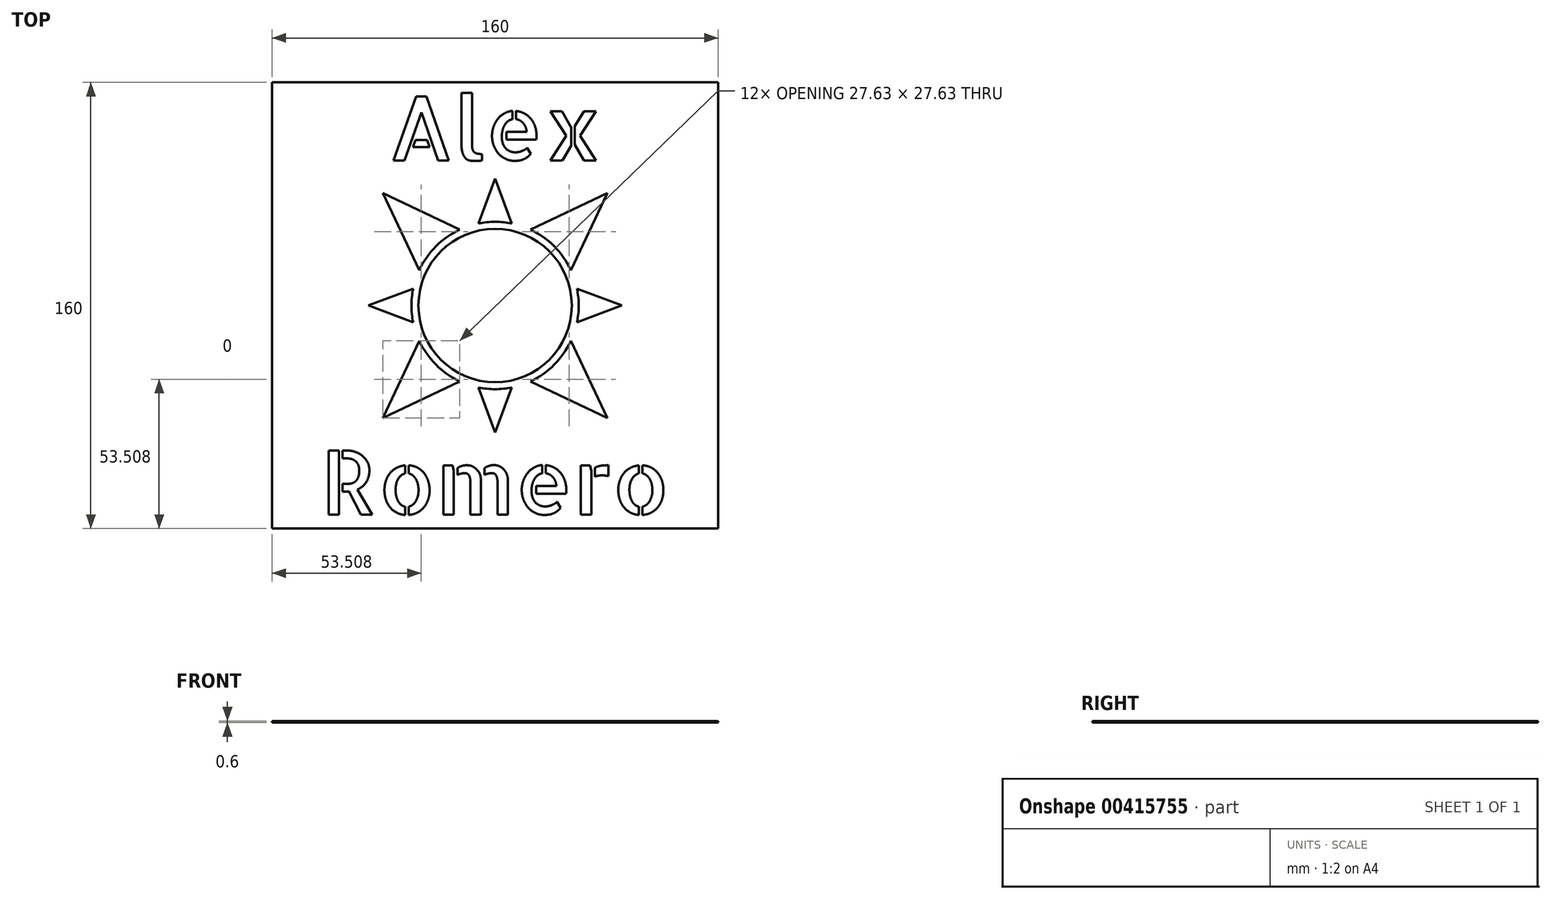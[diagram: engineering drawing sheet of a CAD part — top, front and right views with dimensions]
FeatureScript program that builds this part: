
annotation { "Feature Type Name" : "Feature", "Feature Type Description" : "" }
export const myFeature = defineFeature(function(context is Context, id is Id, definition is map)
    precondition{}
    {
        {
            var Q0;
            Q0=qCreatedBy(makeId("Top.planeOp"),FACE);
            var sketch = newSketch(context, id + "F0", { "sketchPlane" : qUnion([Q0])});
            skLineSegment(sketch, "E0.bottom", {"start": v(0, 0) * mm, "end": v(160, 0) * mm});
            skLineSegment(sketch, "E0.top", {"start": v(0, 160) * mm, "end": v(160, 160) * mm});
            skLineSegment(sketch, "E0.left", {"start": v(0, 0) * mm, "end": v(0, 160) * mm});
            skLineSegment(sketch, "E0.right", {"start": v(160, 0) * mm, "end": v(160, 160) * mm});
            skCircle(sketch, "E1", {"center": v(80, 80) * mm, "radius": 27.5 * mm});
            skLineSegment(sketch, "E2", {"start": v(0, 80) * mm, "end": v(160, 80) * mm, "construction": true});
            skLineSegment(sketch, "E3", {"start": v(80, 0) * mm, "end": v(80, 160) * mm, "construction": true});
            skText(sketch, "E4", { "text": "Alex", "fontName": "AllertaStencil-Regular.ttf"});
            skText(sketch, "E5", { "text": "Romero", "fontName": "AllertaStencil-Regular.ttf"});
            skArc(sketch, "E6", {"start": v(74, 109.4) * mm, "mid": v(80, 110) * mm, "end": v(86, 109.4) * mm});
            skLineSegment(sketch, "E7", {"start": v(74, 109.4) * mm, "end": v(80, 125.5) * mm});
            skLineSegment(sketch, "E8", {"start": v(80, 125.5) * mm, "end": v(86, 109.4) * mm});
            skLineSegment(sketch, "E9.1.0", {"start": v(109.4, 86) * mm, "end": v(125.5, 80) * mm});
            skLineSegment(sketch, "E9.1.1", {"start": v(125.5, 80) * mm, "end": v(109.4, 74) * mm});
            skArc(sketch, "E9.1.2", {"start": v(109.4, 86) * mm, "mid": v(110, 80) * mm, "end": v(109.4, 74) * mm});
            skLineSegment(sketch, "E9.2.0", {"start": v(86, 50.6) * mm, "end": v(80, 34.5) * mm});
            skLineSegment(sketch, "E9.2.1", {"start": v(80, 34.5) * mm, "end": v(74, 50.6) * mm});
            skArc(sketch, "E9.2.2", {"start": v(86, 50.6) * mm, "mid": v(80, 50) * mm, "end": v(74, 50.6) * mm});
            skLineSegment(sketch, "E9.3.0", {"start": v(50.6, 74) * mm, "end": v(34.5, 80) * mm});
            skLineSegment(sketch, "E9.3.1", {"start": v(34.5, 80) * mm, "end": v(50.6, 86) * mm});
            skArc(sketch, "E9.3.2", {"start": v(50.6, 74) * mm, "mid": v(50, 80) * mm, "end": v(50.6, 86) * mm});
            skLineSegment(sketch, "E9.anchor1", {"start": v(80, 80) * mm, "end": v(74, 109.4) * mm, "construction": true});
            skLineSegment(sketch, "E9.anchor2", {"start": v(80, 80) * mm, "end": v(50.6, 74) * mm, "construction": true});
            skLineSegment(sketch, "E10", {"start": v(80, 80) * mm, "end": v(33.62, 126.38) * mm, "construction": true});
            skLineSegment(sketch, "E11", {"start": v(80, 80) * mm, "end": v(42.08, 97.68) * mm, "construction": true});
            skLineSegment(sketch, "E12", {"start": v(80, 80) * mm, "end": v(62.27, 118.03) * mm, "construction": true});
            skArc(sketch, "E13", {"start": v(52.81, 92.68) * mm, "mid": v(58.79, 101.21) * mm, "end": v(67.32, 107.19) * mm});
            skLineSegment(sketch, "E14", {"start": v(52.81, 92.68) * mm, "end": v(39.7, 120.3) * mm});
            skLineSegment(sketch, "E15", {"start": v(39.7, 120.3) * mm, "end": v(67.32, 107.19) * mm});
            skLineSegment(sketch, "E16.1.0", {"start": v(67.32, 52.81) * mm, "end": v(39.7, 39.7) * mm});
            skLineSegment(sketch, "E16.1.1", {"start": v(39.7, 39.7) * mm, "end": v(52.81, 67.32) * mm});
            skArc(sketch, "E16.1.2", {"start": v(67.32, 52.81) * mm, "mid": v(58.79, 58.79) * mm, "end": v(52.81, 67.32) * mm});
            skLineSegment(sketch, "E16.2.0", {"start": v(107.19, 67.32) * mm, "end": v(120.3, 39.7) * mm});
            skLineSegment(sketch, "E16.2.1", {"start": v(120.3, 39.7) * mm, "end": v(92.68, 52.81) * mm});
            skArc(sketch, "E16.2.2", {"start": v(107.19, 67.32) * mm, "mid": v(101.21, 58.79) * mm, "end": v(92.68, 52.81) * mm});
            skLineSegment(sketch, "E16.3.0", {"start": v(92.68, 107.19) * mm, "end": v(120.3, 120.3) * mm});
            skLineSegment(sketch, "E16.3.1", {"start": v(120.3, 120.3) * mm, "end": v(107.19, 92.68) * mm});
            skArc(sketch, "E16.3.2", {"start": v(92.68, 107.19) * mm, "mid": v(101.21, 101.21) * mm, "end": v(107.19, 92.68) * mm});
            skLineSegment(sketch, "E16.anchor1", {"start": v(80, 80) * mm, "end": v(52.81, 92.68) * mm, "construction": true});
            skLineSegment(sketch, "E16.anchor2", {"start": v(80, 80) * mm, "end": v(92.68, 107.19) * mm, "construction": true});
            const initialGuessF0  = {"E4": [0.04165, 0.132, 1, 0, 0.023], "E5": [0.01747, 0.005, 1, 0, 0.023]};
            skSetInitialGuess(sketch, initialGuessF0);
            skSolve(sketch);
        }
        {
            var Q0;
            Q0=makeQuery(id+"F0.imprint","IMPRINT",FACE,{"disambiguationData":[TD([[makeQuery(id+"F0.imprint","IMPRINT",EDGE,{"derivedFrom":sQuery(id+"F0.wireOp",EDGE,"E0.bottom")}),1.0]])]});
            extrude(context, id + "F1", {"entities" : qUnion([Q0]), "depth" : 0.6 * mm});
        }
    });
